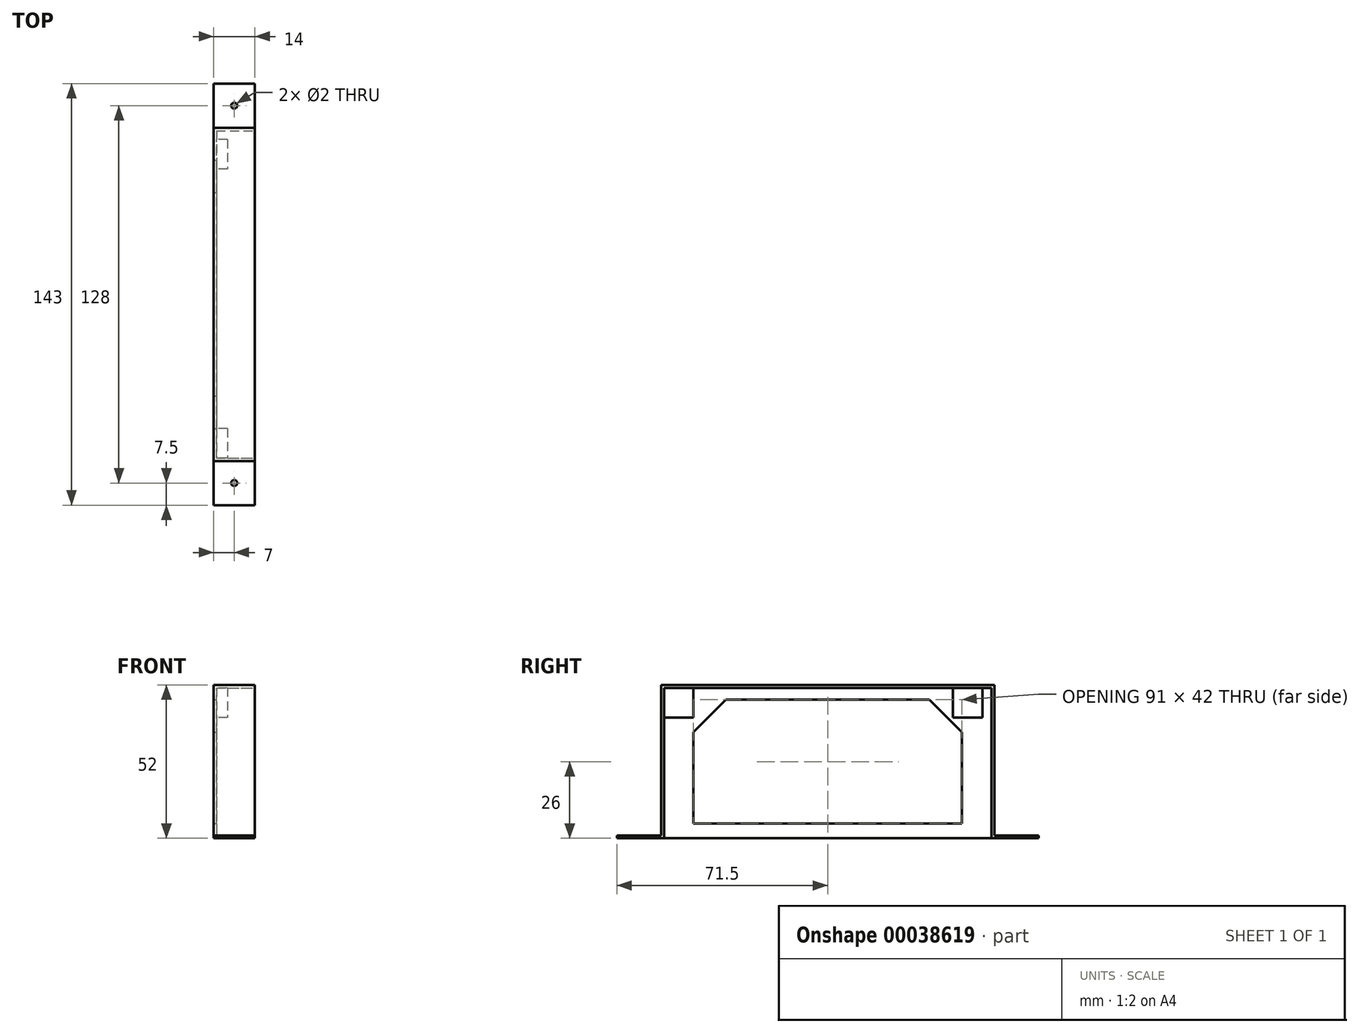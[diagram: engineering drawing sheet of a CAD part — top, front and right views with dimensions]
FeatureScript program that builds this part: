
annotation { "Feature Type Name" : "Feature", "Feature Type Description" : "" }
export const myFeature = defineFeature(function(context is Context, id is Id, definition is map)
    precondition{}
    {
        {
            var Q0;
            Q0=qCreatedBy(makeId("Top.planeOp"),FACE);
            var sketch = newSketch(context, id + "F0", { "sketchPlane" : qUnion([Q0])});
            skLineSegment(sketch, "E0.bottom", {"start": v(-14, 56.5) * mm, "end": v(0, 56.5) * mm});
            skLineSegment(sketch, "E0.top", {"start": v(-14, -56.5) * mm, "end": v(0, -56.5) * mm});
            skLineSegment(sketch, "E0.left", {"start": v(-14, 56.5) * mm, "end": v(-14, -56.5) * mm});
            skLineSegment(sketch, "E0.right", {"start": v(0, 56.5) * mm, "end": v(0, -56.5) * mm});
            skSolve(sketch);
        }
        {
            var Q0;
            Q0=qSketchRegion(id+"F0",true);
            extrude(context, id + "F1", {"entities" : qUnion([Q0]), "depth" : 52 * mm});
        }
        {
            var Q0;
            Q0=makeQuery(id+"F1.opExtrude","CAP_FACE",FACE,{"disambiguationData":[OSD([sQuery(id+"F0.wireOp",EDGE,"E0.bottom"),sQuery(id+"F0.wireOp",EDGE,"E0.top"),sQuery(id+"F0.wireOp",EDGE,"E0.left"),sQuery(id+"F0.wireOp",EDGE,"E0.right")])],"isStart":true});
            var sketch = newSketch(context, id + "F2", { "sketchPlane" : qUnion([Q0])});
            skLineSegment(sketch, "E1.bottom", {"start": v(-13, -55.5) * mm, "end": v(0, -55.5) * mm});
            skLineSegment(sketch, "E1.top", {"start": v(-13, 55.5) * mm, "end": v(0, 55.5) * mm});
            skLineSegment(sketch, "E1.left", {"start": v(-13, -55.5) * mm, "end": v(-13, 55.5) * mm});
            skLineSegment(sketch, "E1.right", {"start": v(0, -55.5) * mm, "end": v(0, 55.5) * mm});
            skSolve(sketch);
        }
        {
            var Q0;
            Q0 = qSketchRegion(id + "F2", true);
            extrude(context, id + "F3", {"entities" : qUnion([Q0]), "operationType" : NewBodyOperationType.REMOVE, "oppositeDirection" : true, "depth" : 51 * mm});
        }
        {
            var Q0;
            Q0=qCreatedBy(makeId("Top.planeOp"),FACE);
            var sketch = newSketch(context, id + "F4", { "sketchPlane" : qUnion([Q0])});
            skLineSegment(sketch, "E2.bottom", {"start": v(0, 56.5) * mm, "end": v(-14, 56.5) * mm});
            skLineSegment(sketch, "E2.top", {"start": v(0, 71.5) * mm, "end": v(-14, 71.5) * mm});
            skLineSegment(sketch, "E2.left", {"start": v(0, 56.5) * mm, "end": v(0, 71.5) * mm});
            skLineSegment(sketch, "E2.right", {"start": v(-14, 56.5) * mm, "end": v(-14, 71.5) * mm});
            skLineSegment(sketch, "E3.bottom", {"start": v(-14, -71.5) * mm, "end": v(0, -71.5) * mm});
            skLineSegment(sketch, "E3.top", {"start": v(-14, -56.5) * mm, "end": v(0, -56.5) * mm});
            skLineSegment(sketch, "E3.left", {"start": v(-14, -71.5) * mm, "end": v(-14, -56.5) * mm});
            skLineSegment(sketch, "E3.right", {"start": v(0, -71.5) * mm, "end": v(0, -56.5) * mm});
            skCircle(sketch, "E4", {"center": v(-7, -64) * mm, "radius": 1 * mm});
            skCircle(sketch, "E5", {"center": v(-7, 64) * mm, "radius": 1 * mm});
            skLineSegment(sketch, "E6", {"start": v(-7, -71.5) * mm, "end": v(-7, -56.5) * mm, "construction": true});
            skLineSegment(sketch, "E7", {"start": v(-14, -64) * mm, "end": v(-7, -64) * mm, "construction": true});
            skLineSegment(sketch, "E8", {"start": v(-7, -64) * mm, "end": v(0, -64) * mm, "construction": true});
            skLineSegment(sketch, "E9", {"start": v(-7, 56.5) * mm, "end": v(-7, 71.5) * mm, "construction": true});
            skLineSegment(sketch, "E10", {"start": v(-14, 64) * mm, "end": v(-7, 64) * mm, "construction": true});
            skLineSegment(sketch, "E11", {"start": v(-7, 64) * mm, "end": v(0, 64) * mm, "construction": true});
            skSolve(sketch);
        }
        {
            var Q0;
            Q0=qSketchRegion(id+"F4",true);
            extrude(context, id + "F5", {"entities" : qUnion([Q0]), "operationType" : NewBodyOperationType.ADD, "depth" : 1 * mm});
        }
        {
            var Q0;
            Q0=makeQuery(id+"F3.boolean.opBoolean","COPY",FACE,{"derivedFrom":makeQuery(id+"F3.opExtrude","SWEPT_FACE",FACE,{"disambiguationData":[OSD([sQuery(id+"F2.wireOp",EDGE,"E1.left")])]})});
            var sketch = newSketch(context, id + "F6", { "sketchPlane" : qUnion([Q0])});
            skLineSegment(sketch, "E12", {"start": v(-45.5, 5) * mm, "end": v(-45.5, 36) * mm});
            skLineSegment(sketch, "E13", {"start": v(-45.5, 36) * mm, "end": v(-34.5, 47) * mm});
            skLineSegment(sketch, "E14", {"start": v(-34.5, 47) * mm, "end": v(34.5, 47) * mm});
            skLineSegment(sketch, "E15", {"start": v(34.5, 47) * mm, "end": v(45.5, 36) * mm});
            skLineSegment(sketch, "E16", {"start": v(45.5, 36) * mm, "end": v(45.5, 5) * mm});
            skLineSegment(sketch, "E17", {"start": v(45.5, 5) * mm, "end": v(-45.5, 5) * mm});
            skLineSegment(sketch, "E18", {"start": v(-55.5, 36) * mm, "end": v(55.5, 36) * mm, "construction": true});
            skSolve(sketch);
        }
        {
            var Q0;
            Q0 = qSketchRegion(id + "F6", true);
            extrude(context, id + "F7", {"entities" : qUnion([Q0]), "operationType" : NewBodyOperationType.REMOVE, "oppositeDirection" : true, "depth" : 1 * mm});
        }
        {
            var Q0;
            Q0=makeQuery(id+"F3.boolean.opBoolean","COPY",FACE,{"derivedFrom":makeQuery(id+"F3.opExtrude","SWEPT_FACE",FACE,{"disambiguationData":[OSD([sQuery(id+"F2.wireOp",EDGE,"E1.left")])]})});
            var sketch = newSketch(context, id + "F8", { "sketchPlane" : qUnion([Q0])});
            skLineSegment(sketch, "E19.bottom", {"start": v(-55.5, 51) * mm, "end": v(-45.5, 51) * mm});
            skLineSegment(sketch, "E19.top", {"start": v(-55.5, 41) * mm, "end": v(-45.5, 41) * mm});
            skLineSegment(sketch, "E19.left", {"start": v(-55.5, 51) * mm, "end": v(-55.5, 41) * mm});
            skLineSegment(sketch, "E19.right", {"start": v(-45.5, 51) * mm, "end": v(-45.5, 41) * mm});
            skPoint(sketch, "E20.oppositeSnap0", {"position": v(-40, 41.5) * mm});
            skLineSegment(sketch, "E21", {"start": v(-55.5, 41) * mm, "end": v(55.5, 41) * mm, "construction": true});
            skLineSegment(sketch, "E22.bottom", {"start": v(42.5, 41) * mm, "end": v(52.5, 41) * mm});
            skLineSegment(sketch, "E22.top", {"start": v(42.5, 51) * mm, "end": v(52.5, 51) * mm});
            skLineSegment(sketch, "E22.left", {"start": v(42.5, 41) * mm, "end": v(42.5, 51) * mm});
            skLineSegment(sketch, "E22.right", {"start": v(52.5, 41) * mm, "end": v(52.5, 51) * mm});
            skSolve(sketch);
        }
        {
            var Q0;
            Q0 = qSketchRegion(id + "F8", true);
            var Q1;
            Q1 = qSketchRegion(id + "F8", true);
            extrude(context, id + "F9", {"entities" : qUnion([Q0, Q1]), "operationType" : NewBodyOperationType.ADD, "depth" : 3.7 * mm});
        }
    });
